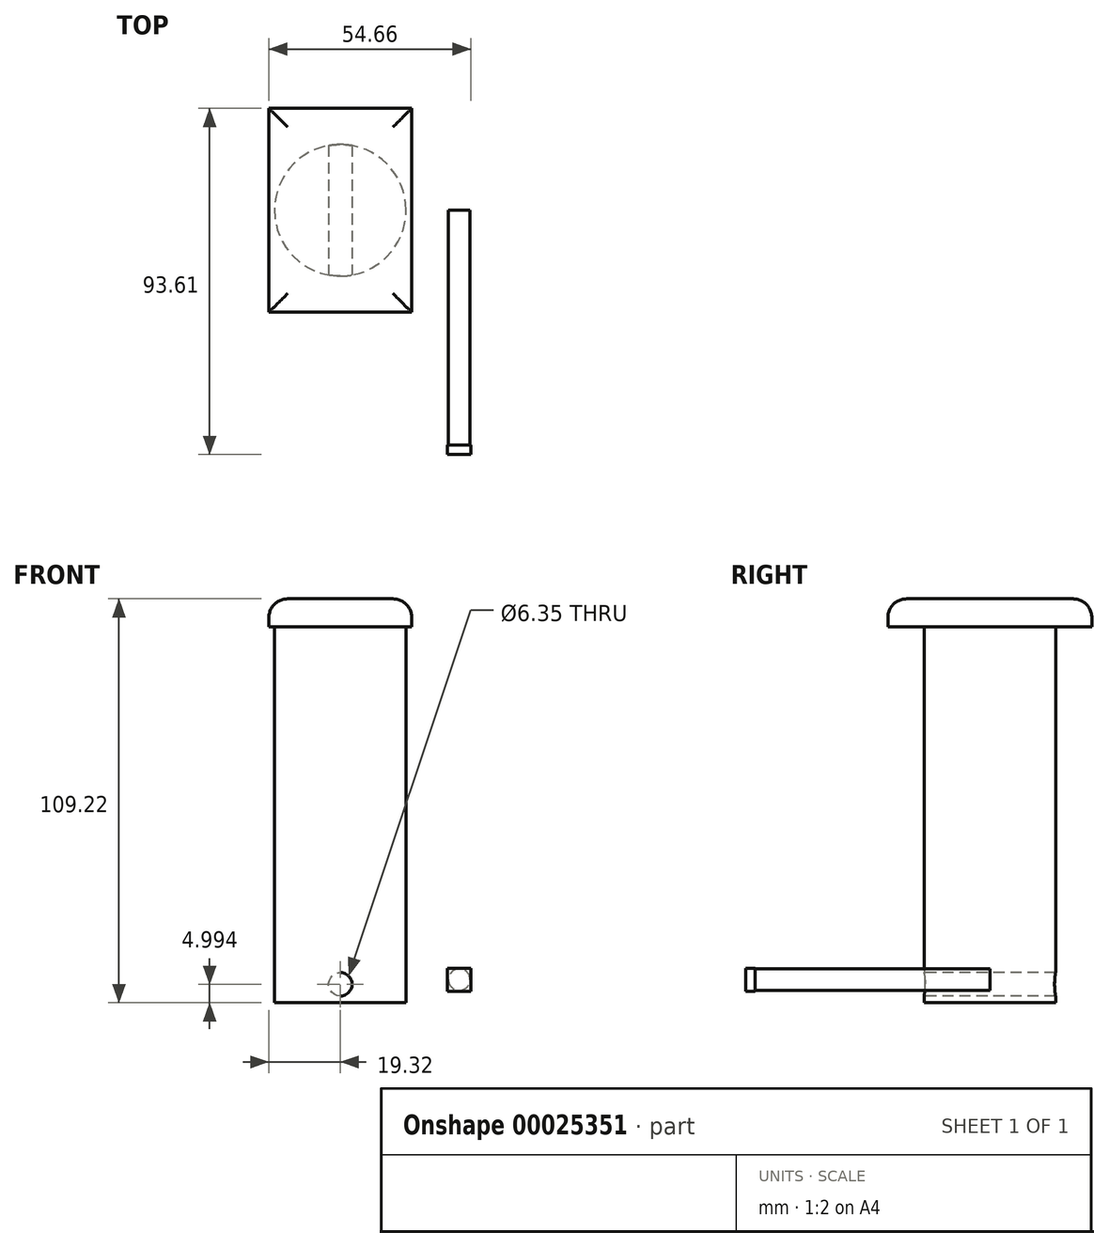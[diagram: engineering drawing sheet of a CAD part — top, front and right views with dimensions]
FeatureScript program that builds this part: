
annotation { "Feature Type Name" : "Feature", "Feature Type Description" : "" }
export const myFeature = defineFeature(function(context is Context, id is Id, definition is map)
    precondition{}
    {
        {
            var Q0;
            Q0=qCreatedBy(makeId("Top.planeOp"),FACE);
            var sketch = newSketch(context, id + "F0", { "sketchPlane" : qUnion([Q0])});
            skCircle(sketch, "E0", {"center": v(0, 0) * mm, "radius": 17.78 * mm});
            skSolve(sketch);
        }
        {
            var Q0;
            Q0=makeQuery(id+"F0.imprint","IMPRINT",FACE,{"disambiguationData":[TD([[makeQuery(id+"F0.imprint","IMPRINT",EDGE,{"derivedFrom":sQuery(id+"F0.wireOp",EDGE,"E0")}),1.0]])]});
            extrude(context, id + "F1", {"entities" : qUnion([Q0]), "depth" : 101.6 * mm});
        }
        {
            var Q0;
            Q0=qCreatedBy(makeId("Front.planeOp"),FACE);
            var sketch = newSketch(context, id + "F2", { "sketchPlane" : qUnion([Q0])});
            skCircle(sketch, "E1", {"center": v(0, 5) * mm, "radius": 3.17 * mm});
            skSolve(sketch);
        }
        {
            var Q0;
            Q0 = qSketchRegion(id + "F2", true);
            extrude(context, id + "F3", {"entities" : qUnion([Q0]), "operationType" : NewBodyOperationType.ADD, "depth" : 19.05 * mm});
        }
        {
            var Q0;
            Q0=makeQuery(id+"F3.opExtrude","CAP_FACE",FACE,{"disambiguationData":[OSD([sQuery(id+"F2.wireOp",EDGE,"E1")])],"isStart":false});
            var sketch = newSketch(context, id + "F4", { "sketchPlane" : qUnion([Q0])});
            skCircle(sketch, "E2", {"center": v(0, 5) * mm, "radius": 3.17 * mm});
            skSolve(sketch);
        }
        {
            var Q0;
            Q0=sQuery(id+"F4.wireOp",VERTEX,"E2.center");
            var Q1;
            Q1=makeQuery(id+"F1.opExtrude","SWEPT_BODY",BODY,{"disambiguationData":[OSD([sQuery(id+"F0.wireOp",EDGE,"E0")])]});
            hole(context, id + "F5", {"style" : HoleStyle.SIMPLE, "holeDiameter" : 6.35 * mm, "endStyle" : HoleEndStyle.THROUGH, "locations" : qUnion([Q0]), "scope" : qUnion([Q1])});
        }
        {
            var Q0;
            Q0=makeQuery(id+"F1.opExtrude","CAP_FACE",FACE,{"disambiguationData":[OSD([sQuery(id+"F0.wireOp",EDGE,"E0")])],"isStart":false});
            var sketch = newSketch(context, id + "F6", { "sketchPlane" : qUnion([Q0])});
            skLineSegment(sketch, "E3.rect.bottom", {"start": v(19.32, 27.57) * mm, "end": v(-19.32, 27.57) * mm});
            skLineSegment(sketch, "E3.rect.top", {"start": v(19.32, -27.57) * mm, "end": v(-19.32, -27.57) * mm});
            skLineSegment(sketch, "E3.rect.left", {"start": v(19.32, 27.57) * mm, "end": v(19.32, -27.57) * mm});
            skLineSegment(sketch, "E3.rect.right", {"start": v(-19.32, 27.57) * mm, "end": v(-19.32, -27.57) * mm});
            skPoint(sketch, "E3.rect.middle", {"position": v(0, 0) * mm});
            skSolve(sketch);
        }
        {
            var Q0;
            Q0=makeQuery(id+"F6.imprint","IMPRINT",FACE,{"disambiguationData":[TD([[makeQuery(id+"F6.imprint","IMPRINT",EDGE,{"derivedFrom":makeQuery(id+"F1.opExtrude","CAP_EDGE",EDGE,{"disambiguationData":[OSD([sQuery(id+"F0.wireOp",EDGE,"E0")])],"isStart":false})}),1.0]])]});
            var Q1;
            Q1=makeQuery(id+"F6.imprint","IMPRINT",FACE,{"disambiguationData":[TD([[makeQuery(id+"F6.imprint","IMPRINT",EDGE,{"derivedFrom":sQuery(id+"F6.wireOp",EDGE,"E3.rect.bottom")}),1.0]])]});
            extrude(context, id + "F7", {"entities" : qUnion([Q0, Q1]), "operationType" : NewBodyOperationType.ADD, "depth" : 7.62 * mm});
        }
        {
            var Q0;
            Q0=makeQuery(id+"F7.opExtrude","CAP_EDGE",EDGE,{"disambiguationData":[OSD([sQuery(id+"F6.wireOp",EDGE,"E3.rect.top")])],"isStart":false});
            var Q1;
            Q1=makeQuery(id+"F7.opExtrude","CAP_EDGE",EDGE,{"disambiguationData":[OSD([sQuery(id+"F6.wireOp",EDGE,"E3.rect.right")])],"isStart":false});
            var Q2;
            Q2=makeQuery(id+"F7.opExtrude","CAP_EDGE",EDGE,{"disambiguationData":[OSD([sQuery(id+"F6.wireOp",EDGE,"E3.rect.bottom")])],"isStart":false});
            var Q3;
            Q3=makeQuery(id+"F7.opExtrude","CAP_EDGE",EDGE,{"disambiguationData":[OSD([sQuery(id+"F6.wireOp",EDGE,"E3.rect.left")])],"isStart":false});
            fillet(context, id + "F8", {"entities" : qUnion([Q0, Q1, Q2, Q3]), "radius" : 5.08 * mm, "tangentPropagation" : true, "allowEdgeOverflow" : false});
        }
        {
            var Q0;
            Q0=qCreatedBy(makeId("Front.planeOp"),FACE);
            var sketch = newSketch(context, id + "F9", { "sketchPlane" : qUnion([Q0])});
            skCircle(sketch, "E4", {"center": v(32.16, 6.25) * mm, "radius": 2.92 * mm});
            skSolve(sketch);
        }
        {
            var Q0;
            Q0=makeQuery(id+"F9.imprint","IMPRINT",FACE,{"disambiguationData":[TD([[makeQuery(id+"F9.imprint","IMPRINT",EDGE,{"derivedFrom":sQuery(id+"F9.wireOp",EDGE,"E4")}),1.0]])]});
            extrude(context, id + "F10", {"entities" : qUnion([Q0]), "depth" : 63.5 * mm});
        }
        {
            var Q0;
            Q0=makeQuery(id+"F10.opExtrude","CAP_FACE",FACE,{"disambiguationData":[OSD([sQuery(id+"F9.wireOp",EDGE,"E4")])],"isStart":false});
            var sketch = newSketch(context, id + "F11", { "sketchPlane" : qUnion([Q0])});
            skLineSegment(sketch, "E5.rect.bottom", {"start": v(35.34, 9.36) * mm, "end": v(28.98, 9.36) * mm});
            skLineSegment(sketch, "E5.rect.top", {"start": v(35.34, 3.14) * mm, "end": v(28.98, 3.14) * mm});
            skLineSegment(sketch, "E5.rect.left", {"start": v(35.34, 9.36) * mm, "end": v(35.34, 3.14) * mm});
            skLineSegment(sketch, "E5.rect.right", {"start": v(28.98, 9.36) * mm, "end": v(28.98, 3.14) * mm});
            skPoint(sketch, "E5.rect.middle", {"position": v(32.16, 6.25) * mm});
            skSolve(sketch);
        }
        {
            var Q0;
            Q0=makeQuery(id+"F11.imprint","IMPRINT",FACE,{"disambiguationData":[TD([[makeQuery(id+"F11.imprint","IMPRINT",EDGE,{"derivedFrom":makeQuery(id+"F10.opExtrude","CAP_EDGE",EDGE,{"disambiguationData":[OSD([sQuery(id+"F9.wireOp",EDGE,"E4")])],"isStart":false})}),1.0]])]});
            var Q1;
            Q1=makeQuery(id+"F11.imprint","IMPRINT",FACE,{"disambiguationData":[TD([[makeQuery(id+"F11.imprint","IMPRINT",EDGE,{"derivedFrom":sQuery(id+"F11.wireOp",EDGE,"E5.rect.bottom")}),1.0]])]});
            extrude(context, id + "F12", {"entities" : qUnion([Q0, Q1]), "operationType" : NewBodyOperationType.ADD, "depth" : 2.54 * mm});
        }
    });
